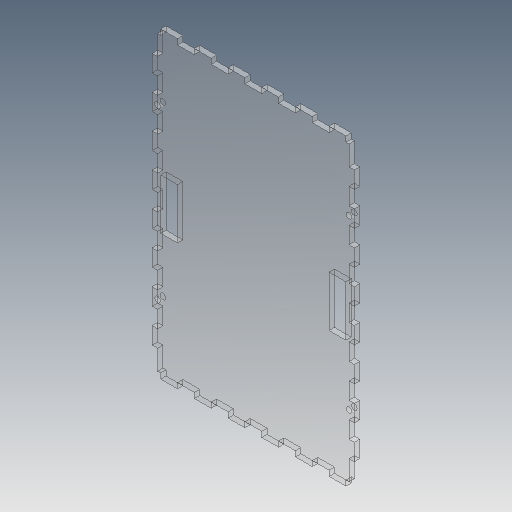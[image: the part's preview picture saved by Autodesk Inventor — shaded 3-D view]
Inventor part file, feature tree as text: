
AUTODESK INVENTOR PART (.ipt)
format: ipt  version: 2018 (Build 220112000, 112)  size: 348,160 bytes
history: native  units: mm
features: sketch x8, extrude x6, mirror x5, projected_geometry x5, pattern_linear x2, hole x2
ambient origin geometry x8: Origin, YZ Plane, XZ Plane, XY Plane, X Axis, Y Axis, Z Axis, Center Point
bodies: Solid1 (feature_tree)
feature tree (28):
  extrude  "Extrusion1"  Depth=180.0mm
  extrude  "Extrusion3"  TaperAngle=0.0deg  [1 undecoded]
  pattern_linear  "Rectangular Pattern1"  Count1=4  [1 undecoded]
  extrude  "Extrusion5"  Depth=15.0mm
  mirror  "Mirror1"
  extrude  "Extrusion4"  Depth=15.0mm
  pattern_linear  "Rectangular Pattern2"  Spacing1=10.0mm  [1 undecoded]
  extrude  "Extrusion6"  Depth=15.0mm
  mirror  "Mirror2"
  hole  "Hole2"  [1 undecoded]
  mirror  "Mirror3"
  mirror  "Mirror4"
  extrude  "Extrusion7"  Depth=10.0mm TaperAngle=0.0deg
  mirror  "Mirror5"
  hole  "Hole1"  [1 undecoded]
  sketch  "Sketch1"  dims[d0=120.0mm d1=180.0mm]
  sketch  "Sketch3"  dims[d2=3.175mm d3=0.0mm]
  projected_geometry  "Projected Loop1"
  sketch  "Sketch4"  dims[d9=1.5875mm]
  projected_geometry  "Projected Loop2"
  sketch  "Sketch5"  dims[d10=1.5875mm]
  projected_geometry  "Projected Loop3"
  sketch  "Sketch6"  dims[d11=1.5875mm]
  sketch  "Sketch7"  dims[d12=1.5875mm]
  projected_geometry  "Projected Loop4"
  sketch  "Sketch8"  dims[d13=3.0mm d14=6.0mm d15=4.0mm d16=2.0mm d17=90.0deg d18=8.0mm d19=20.594885mm d20=40.0mm]
  projected_geometry  "Projected Loop5"
  sketch  "Sketch9"  dims[d21=40.0mm d22=36.0mm d24=36.0mm d25=10.0mm d26=15.0mm d27=3.175mm d28=10.0mm d29=0.0mm d30=60.0mm d32=20.0mm d33=3.175mm d34=5.0mm d35=10.0mm d36=0.0mm d37=0.0mm d38=90.0mm d40=20.0mm d41=50.0mm d42=56.825mm d43=3.4mm d44=6.0mm d45=6.3mm d46=2.0mm d47=90.0deg d48=8.0mm d49=20.594885mm d50=10.0mm d51=3.175mm d52=10.0mm d53=0.0mm d54=10.0mm d55=0.0mm d56=30.0mm d57=10.0mm d58=45.0mm d60=10.0mm d61=0.0mm d62=15.0mm]
note: 5 required parameter values undecoded (feature->parameter linkage not recoverable at this tier; creation-order binding heuristic only, values carry confidence <= 0.55)
